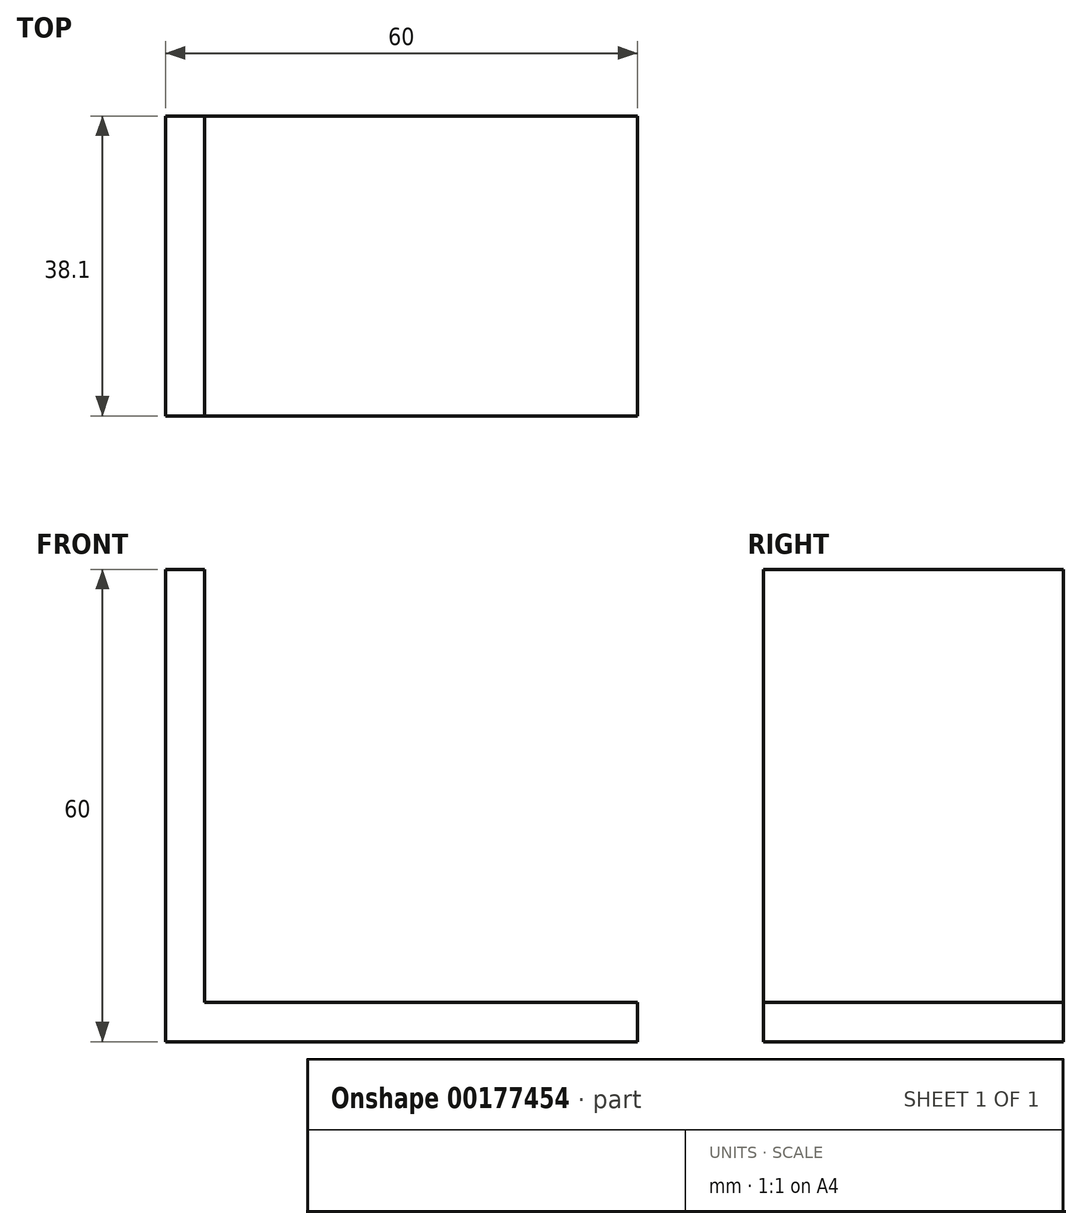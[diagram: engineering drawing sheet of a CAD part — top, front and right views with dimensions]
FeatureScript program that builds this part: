
annotation { "Feature Type Name" : "Feature", "Feature Type Description" : "" }
export const myFeature = defineFeature(function(context is Context, id is Id, definition is map)
    precondition{}
    {
        {
            var Q0;
            Q0=qCreatedBy(makeId("Front.planeOp"),FACE);
            var sketch = newSketch(context, id + "F0", { "sketchPlane" : qUnion([Q0])});
            skLineSegment(sketch, "E0", {"start": v(0, 0) * mm, "end": v(60, 0) * mm});
            skLineSegment(sketch, "E1", {"start": v(0, 0) * mm, "end": v(0, 60) * mm});
            skLineSegment(sketch, "E2.0", {"start": v(5, 5) * mm, "end": v(5, 60) * mm});
            skLineSegment(sketch, "E2.1", {"start": v(5, 5) * mm, "end": v(60, 5) * mm});
            skLineSegment(sketch, "E3", {"start": v(0, 60) * mm, "end": v(5, 60) * mm});
            skLineSegment(sketch, "E4", {"start": v(60, 0) * mm, "end": v(60, 5) * mm});
            skSolve(sketch);
        }
        {
            var Q0;
            Q0=makeQuery(id+"F0.imprint","IMPRINT",FACE,{"disambiguationData":[TD([[makeQuery(id+"F0.imprint","IMPRINT",EDGE,{"derivedFrom":sQuery(id+"F0.wireOp",EDGE,"E0")}),1.0]])]});
            extrude(context, id + "F1", {"entities" : qUnion([Q0]), "depth" : 38.1 * mm});
        }
    });
